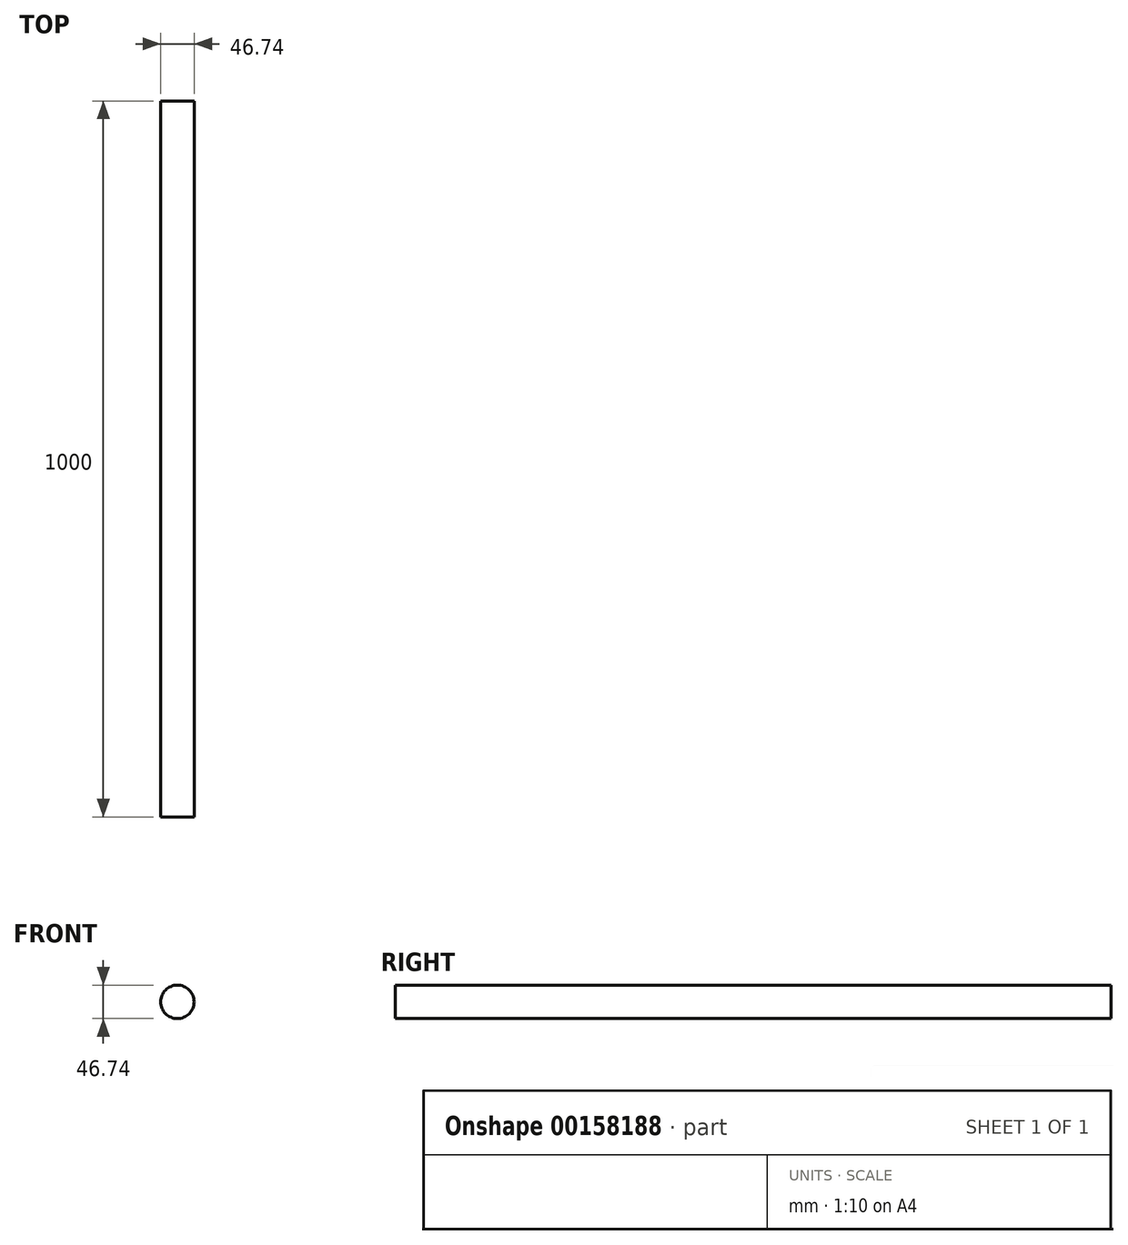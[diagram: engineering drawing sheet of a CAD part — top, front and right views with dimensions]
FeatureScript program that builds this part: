
annotation { "Feature Type Name" : "Feature", "Feature Type Description" : "" }
export const myFeature = defineFeature(function(context is Context, id is Id, definition is map)
    precondition{}
    {
        {
            var Q0;
            Q0=qCreatedBy(makeId("Front.planeOp"),FACE);
            var sketch = newSketch(context, id + "F0", { "sketchPlane" : qUnion([Q0])});
            skCircle(sketch, "E0", {"center": v(0, 0) * mm, "radius": 23.37 * mm});
            skSolve(sketch);
        }
        {
            var Q0;
            Q0=makeQuery(id+"F0.imprint","IMPRINT",FACE,{"disambiguationData":[TD([[makeQuery(id+"F0.imprint","IMPRINT",EDGE,{"derivedFrom":sQuery(id+"F0.wireOp",EDGE,"E0")}),1.0]])]});
            extrude(context, id + "F1", {"entities" : qUnion([Q0]), "depth" : 1000 * mm});
        }
    });
